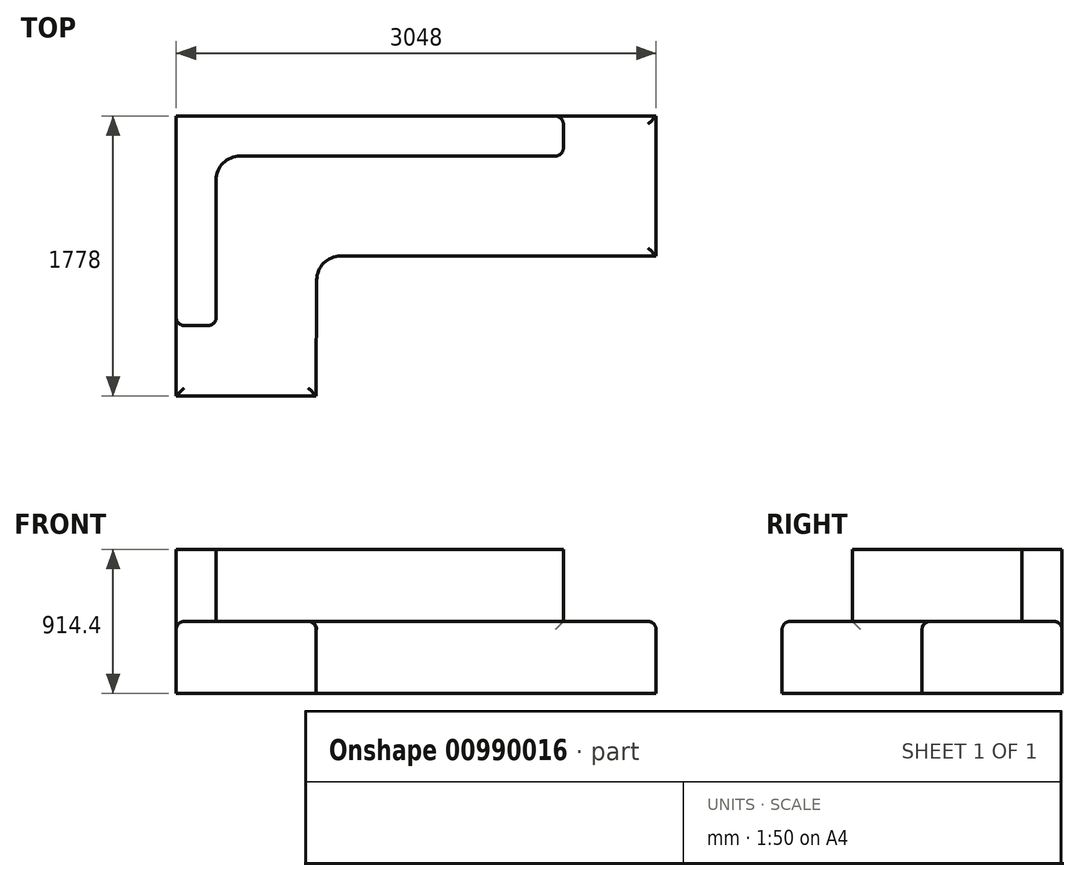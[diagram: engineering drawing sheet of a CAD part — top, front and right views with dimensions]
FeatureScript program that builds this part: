
annotation { "Feature Type Name" : "Feature", "Feature Type Description" : "" }
export const myFeature = defineFeature(function(context is Context, id is Id, definition is map)
    precondition{}
    {
        {
            var Q0;
            Q0=qCreatedBy(makeId("Top.planeOp"),FACE);
            var sketch = newSketch(context, id + "F0", { "sketchPlane" : qUnion([Q0])});
            skLineSegment(sketch, "E0", {"start": v(341.63, -889.8) * mm, "end": v(-547.37, -889.8) * mm});
            skLineSegment(sketch, "E1", {"start": v(-547.37, -889.8) * mm, "end": v(-547.37, 888.2) * mm});
            skLineSegment(sketch, "E2", {"start": v(-547.37, 888.2) * mm, "end": v(2500.63, 888.2) * mm});
            skLineSegment(sketch, "E3", {"start": v(2500.63, 888.2) * mm, "end": v(2500.63, -0.8) * mm});
            skLineSegment(sketch, "E4", {"start": v(2500.63, -0.8) * mm, "end": v(345.7, -0.8) * mm});
            skLineSegment(sketch, "E5", {"start": v(341.63, -889.8) * mm, "end": v(345.7, -0.8) * mm});
            skSolve(sketch);
        }
        {
            var Q0;
            Q0 = qSketchRegion(id + "F0", true);
            extrude(context, id + "F1", {"entities" : qUnion([Q0]), "depth" : 457.2 * mm, "offsetDistance" : 25.4 * mm});
        }
        {
            var Q0;
            Q0=makeQuery(id+"F1.opExtrude","CAP_FACE",FACE,{"disambiguationData":[OSD([sQuery(id+"F0.wireOp",EDGE,"E0"),sQuery(id+"F0.wireOp",EDGE,"E1"),sQuery(id+"F0.wireOp",EDGE,"E2"),sQuery(id+"F0.wireOp",EDGE,"E3"),sQuery(id+"F0.wireOp",EDGE,"E4"),sQuery(id+"F0.wireOp",EDGE,"E5")])],"isStart":false});
            var sketch = newSketch(context, id + "F2", { "sketchPlane" : qUnion([Q0])});
            skLineSegment(sketch, "E6", {"start": v(-547.37, -442.1) * mm, "end": v(-293.37, -442.1) * mm});
            skLineSegment(sketch, "E7", {"start": v(-293.37, -442.1) * mm, "end": v(-293.37, 634.2) * mm});
            skLineSegment(sketch, "E8", {"start": v(-547.37, -442.1) * mm, "end": v(-547.37, 888.2) * mm});
            skLineSegment(sketch, "E9", {"start": v(-547.37, 888.2) * mm, "end": v(1911.57, 888.2) * mm});
            skLineSegment(sketch, "E10", {"start": v(1911.57, 888.2) * mm, "end": v(1911.57, 634.2) * mm});
            skLineSegment(sketch, "E11", {"start": v(1911.57, 634.2) * mm, "end": v(-293.37, 634.2) * mm});
            skSolve(sketch);
        }
        {
            var Q0;
            Q0 = qSketchRegion(id + "F2", true);
            extrude(context, id + "F3", {"entities" : qUnion([Q0]), "operationType" : NewBodyOperationType.ADD, "depth" : 457.2 * mm, "offsetDistance" : 25.4 * mm});
        }
        {
            var Q0;
            Q0=makeQuery(id+"F3.opExtrude","SWEPT_EDGE",EDGE,{"disambiguationData":[OSD([sQuery(id+"F2.wireOp",EDGE,"E7"),sQuery(id+"F2.wireOp",EDGE,"E11")])]});
            var Q1;
            Q1=makeQuery(id+"F1.opExtrude","SWEPT_EDGE",EDGE,{"disambiguationData":[OSD([sQuery(id+"F0.wireOp",EDGE,"E4"),sQuery(id+"F0.wireOp",EDGE,"E5")])]});
            fillet(context, id + "F4", {"entities" : qUnion([Q0, Q1]), "radius" : 152.4 * mm, "tangentPropagation" : true, "allowEdgeOverflow" : false});
        }
        {
            var Q0;
            Q0=makeQuery(id+"F3.opExtrude","SWEPT_EDGE",EDGE,{"disambiguationData":[OSD([sQuery(id+"F2.wireOp",EDGE,"E10"),sQuery(id+"F2.wireOp",EDGE,"E11")])]});
            var Q1;
            Q1=makeQuery(id+"F3.opExtrude","SWEPT_EDGE",EDGE,{"disambiguationData":[OSD([sQuery(id+"F0.wireOp",EDGE,"E2"),sQuery(id+"F2.wireOp",EDGE,"E9"),sQuery(id+"F2.wireOp",EDGE,"E10")])]});
            var Q2;
            Q2=makeQuery(id+"F1.opExtrude","CAP_EDGE",EDGE,{"disambiguationData":[OSD([sQuery(id+"F0.wireOp",EDGE,"E3")])],"isStart":false});
            var Q3;
            Q3=makeQuery(id+"F1.opExtrude","CAP_EDGE",EDGE,{"disambiguationData":[OSD([sQuery(id+"F0.wireOp",EDGE,"E0")])],"isStart":false});
            var Q4;
            Q4=makeQuery(id+"F1.opExtrude","CAP_EDGE",EDGE,{"disambiguationData":[OSD([sQuery(id+"F0.wireOp",EDGE,"E5")])],"isStart":false});
            var Q5;
            Q5=makeQuery(id+"F1.opExtrude","CAP_EDGE",EDGE,{"disambiguationData":[OSD([sQuery(id+"F0.wireOp",EDGE,"E2")])],"isStart":false});
            var Q6;
            Q6=makeQuery(id+"F1.opExtrude","CAP_EDGE",EDGE,{"disambiguationData":[OSD([sQuery(id+"F0.wireOp",EDGE,"E1")])],"isStart":false});
            var Q7;
            Q7=makeQuery(id+"F3.opExtrude","SWEPT_EDGE",EDGE,{"disambiguationData":[OSD([sQuery(id+"F2.wireOp",EDGE,"E6"),sQuery(id+"F2.wireOp",EDGE,"E7")])]});
            var Q8;
            Q8=makeQuery(id+"F3.opExtrude","SWEPT_EDGE",EDGE,{"disambiguationData":[OSD([sQuery(id+"F0.wireOp",EDGE,"E1"),sQuery(id+"F2.wireOp",EDGE,"E6"),sQuery(id+"F2.wireOp",EDGE,"E8")])]});
            fillet(context, id + "F5", {"entities" : qUnion([Q0, Q1, Q2, Q3, Q4, Q5, Q6, Q7, Q8]), "radius" : 50.8 * mm, "tangentPropagation" : true, "allowEdgeOverflow" : false});
        }
    });
